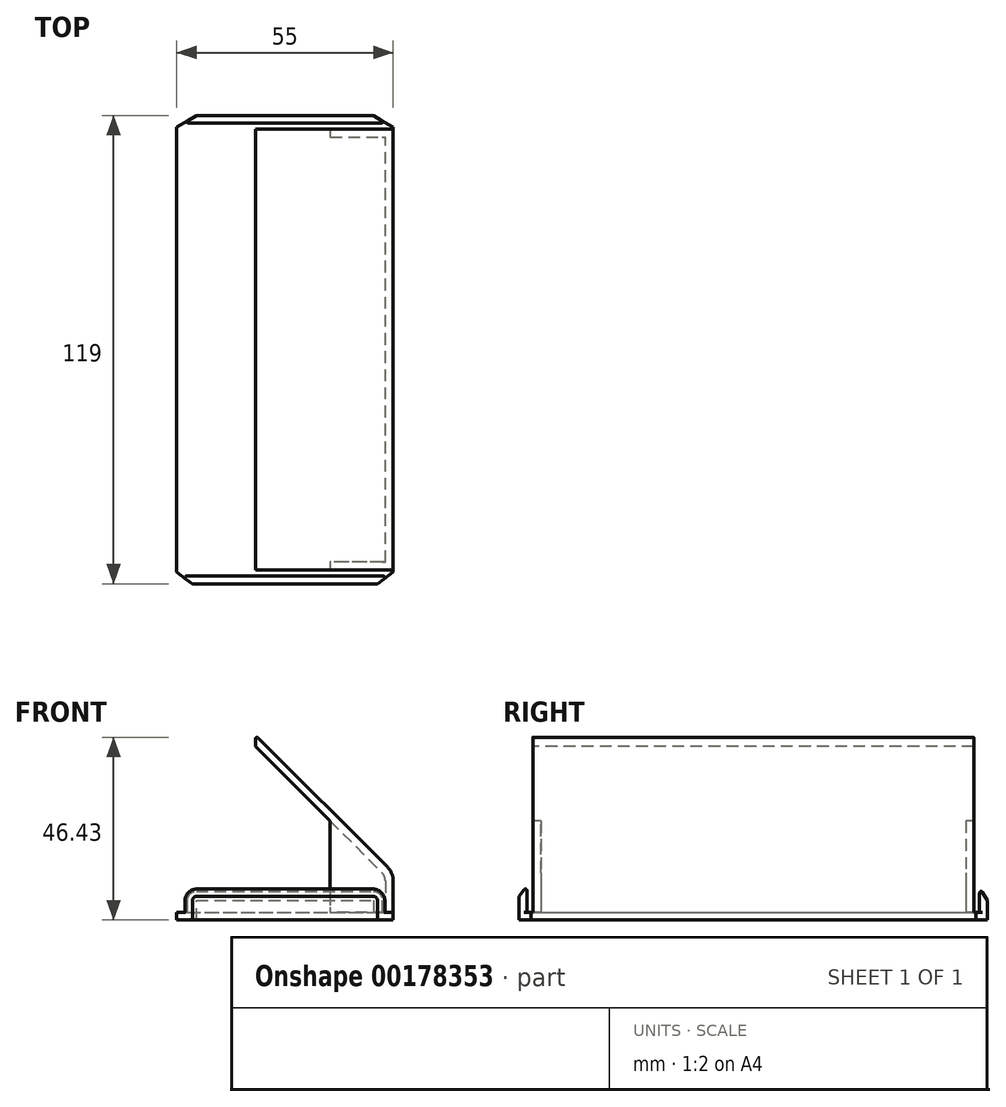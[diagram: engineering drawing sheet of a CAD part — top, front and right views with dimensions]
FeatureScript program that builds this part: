
annotation { "Feature Type Name" : "Feature", "Feature Type Description" : "" }
export const myFeature = defineFeature(function(context is Context, id is Id, definition is map)
    precondition{}
    {
        {
            var Q0;
            Q0=qCreatedBy(makeId("Top.planeOp"),FACE);
            var sketch = newSketch(context, id + "F0", { "sketchPlane" : qUnion([Q0])});
            skLineSegment(sketch, "E0.bottom", {"start": v(27.5, -59.5) * mm, "end": v(-27.5, -59.5) * mm});
            skLineSegment(sketch, "E0.top", {"start": v(27.5, 59.5) * mm, "end": v(-27.5, 59.5) * mm});
            skLineSegment(sketch, "E0.left", {"start": v(27.5, -59.5) * mm, "end": v(27.5, 59.5) * mm});
            skLineSegment(sketch, "E0.right", {"start": v(-27.5, -59.5) * mm, "end": v(-27.5, 59.5) * mm});
            skPoint(sketch, "E0.middle", {"position": v(0, 0) * mm});
            skLineSegment(sketch, "E1", {"start": v(-27.5, 57.5) * mm, "end": v(27.5, 57.5) * mm});
            skLineSegment(sketch, "E2", {"start": v(-27.5, -57.5) * mm, "end": v(27.5, -57.5) * mm});
            skLineSegment(sketch, "E3", {"start": v(-27.5, 56) * mm, "end": v(27.5, 56) * mm});
            skLineSegment(sketch, "E4", {"start": v(-27.5, -56) * mm, "end": v(27.5, -56) * mm});
            skSolve(sketch);
        }
        {
            var Q0;
            {var subQ0=sQuery(id+"F0.wireOp",EDGE,"E3");Q0=makeQuery(id+"F0.imprint","IMPRINT",FACE,{"disambiguationData":[TD([[makeQuery(id+"F0.imprint","IMPRINT",EDGE,{"derivedFrom":subQ0}),-1.0]])]});}
            extrude(context, id + "F1", {"entities" : qUnion([Q0]), "depth" : 47 * mm});
        }
        {
            var Q0;
            {var subQ0=sQuery(id+"F0.wireOp",EDGE,"E1");Q0=makeQuery(id+"F0.imprint","IMPRINT",FACE,{"disambiguationData":[TD([[makeQuery(id+"F0.imprint","IMPRINT",EDGE,{"derivedFrom":subQ0}),-1.0]])]});}
            var Q1;
            {var subQ0=sQuery(id+"F0.wireOp",EDGE,"E2");Q1=makeQuery(id+"F0.imprint","IMPRINT",FACE,{"disambiguationData":[TD([[makeQuery(id+"F0.imprint","IMPRINT",EDGE,{"derivedFrom":subQ0}),1.0]])]});}
            extrude(context, id + "F2", {"entities" : qUnion([Q0, Q1]), "operationType" : NewBodyOperationType.ADD, "depth" : 2 * mm});
        }
        {
            var Q0;
            {var subQ0=sQuery(id+"F0.wireOp",EDGE,"E0.top");Q0=makeQuery(id+"F0.imprint","IMPRINT",FACE,{"disambiguationData":[TD([[makeQuery(id+"F0.imprint","IMPRINT",EDGE,{"derivedFrom":subQ0}),1.0]])]});}
            var Q1;
            {var subQ0=sQuery(id+"F0.wireOp",EDGE,"E0.bottom");Q1=makeQuery(id+"F0.imprint","IMPRINT",FACE,{"disambiguationData":[TD([[makeQuery(id+"F0.imprint","IMPRINT",EDGE,{"derivedFrom":subQ0}),-1.0]])]});}
            extrude(context, id + "F3", {"entities" : qUnion([Q0, Q1]), "operationType" : NewBodyOperationType.ADD, "depth" : 10 * mm});
        }
        {
            var Q0;
            Q0=makeQuery(id+"F1.opExtrude","CAP_EDGE",EDGE,{"disambiguationData":[OSD([sQuery(id+"F0.wireOp",EDGE,"E0.left")])],"isStart":false});
            chamfer(context, id + "F4", {"entities" : qUnion([Q0]), "chamferType" : ChamferType.TWO_OFFSETS, "width1" : 35 * mm, "oppositeDirection" : false, "width2" : 35 * mm, "tangentPropagation" : true});
        }
        {
            var Q0;
            {var subQ0=sQuery(id+"F0.wireOp",EDGE,"E0.right");Q0=makeQuery(id+"F3.opExtrude","CAP_EDGE",EDGE,{"disambiguationData":[OSD([subQ0]),TDD([makeQuery(id+"F0.imprint","IMPRINT",EDGE,{"disambiguationData":[TD([[makeQuery(id+"F0.imprint","INTERSECT",VERTEX,{"derivedFrom":[sQuery(id+"F0.wireOp",EDGE,"E0.bottom"),subQ0]}),-1.0]])],"derivedFrom":subQ0})])],"isStart":false});}
            var Q1;
            {var subQ0=sQuery(id+"F0.wireOp",EDGE,"E0.left");Q1=makeQuery(id+"F3.opExtrude","CAP_EDGE",EDGE,{"disambiguationData":[OSD([subQ0]),TDD([makeQuery(id+"F0.imprint","IMPRINT",EDGE,{"disambiguationData":[TD([[makeQuery(id+"F0.imprint","INTERSECT",VERTEX,{"derivedFrom":[sQuery(id+"F0.wireOp",EDGE,"E0.bottom"),subQ0]}),-1.0]])],"derivedFrom":subQ0})])],"isStart":false});}
            var Q2;
            {var subQ0=sQuery(id+"F0.wireOp",EDGE,"E0.right");Q2=makeQuery(id+"F3.opExtrude","CAP_EDGE",EDGE,{"disambiguationData":[OSD([subQ0]),TDD([makeQuery(id+"F0.imprint","IMPRINT",EDGE,{"disambiguationData":[TD([[makeQuery(id+"F0.imprint","INTERSECT",VERTEX,{"derivedFrom":[sQuery(id+"F0.wireOp",EDGE,"E0.top"),subQ0]}),1.0]])],"derivedFrom":subQ0})])],"isStart":false});}
            var Q3;
            {var subQ0=sQuery(id+"F0.wireOp",EDGE,"E0.left");Q3=makeQuery(id+"F3.opExtrude","CAP_EDGE",EDGE,{"disambiguationData":[OSD([subQ0]),TDD([makeQuery(id+"F0.imprint","IMPRINT",EDGE,{"disambiguationData":[TD([[makeQuery(id+"F0.imprint","INTERSECT",VERTEX,{"derivedFrom":[sQuery(id+"F0.wireOp",EDGE,"E0.top"),subQ0]}),1.0]])],"derivedFrom":subQ0})])],"isStart":false});}
            var Q4;
            {var subQ0=sQuery(id+"F0.wireOp",EDGE,"E0.left");var subQ1=makeQuery(id+"F0.imprint","INTERSECT",VERTEX,{"derivedFrom":[subQ0,sQuery(id+"F0.wireOp",EDGE,"E1")]});var subQ2=makeQuery(id+"F0.imprint","INTERSECT",VERTEX,{"derivedFrom":[subQ0,sQuery(id+"F0.wireOp",EDGE,"E2")]});Q4=makeQuery(id+"F4.opChamfer","BLEND_EDGE",EDGE,{"blendedFrom":[makeQuery(id+"F1.opExtrude","CAP_EDGE",EDGE,{"disambiguationData":[OSD([subQ0])],"isStart":false}),makeQuery(id+"F3.boolean.opBoolean","MERGE",FACE,{"derivedFrom":[makeQuery(id+"F2.boolean.opBoolean","MERGE",FACE,{"derivedFrom":[makeQuery(id+"F1.opExtrude","SWEPT_FACE",FACE,{"disambiguationData":[OSD([subQ0])]}),makeQuery(id+"F2.opExtrude","SWEPT_FACE",FACE,{"disambiguationData":[OSD([subQ0]),TDD([makeQuery(id+"F0.imprint","IMPRINT",EDGE,{"disambiguationData":[TD([[subQ2,-1.0]])],"derivedFrom":subQ0})])]}),makeQuery(id+"F2.opExtrude","SWEPT_FACE",FACE,{"disambiguationData":[OSD([subQ0]),TDD([makeQuery(id+"F0.imprint","IMPRINT",EDGE,{"disambiguationData":[TD([[subQ1,1.0]])],"derivedFrom":subQ0})])]})]}),makeQuery(id+"F3.opExtrude","SWEPT_FACE",FACE,{"disambiguationData":[OSD([subQ0]),TDD([makeQuery(id+"F0.imprint","IMPRINT",EDGE,{"disambiguationData":[TD([[makeQuery(id+"F0.imprint","INTERSECT",VERTEX,{"derivedFrom":[sQuery(id+"F0.wireOp",EDGE,"E0.bottom"),subQ0]}),-1.0]])],"derivedFrom":subQ0})])]}),makeQuery(id+"F3.opExtrude","SWEPT_FACE",FACE,{"disambiguationData":[OSD([subQ0]),TDD([makeQuery(id+"F0.imprint","IMPRINT",EDGE,{"disambiguationData":[TD([[makeQuery(id+"F0.imprint","INTERSECT",VERTEX,{"derivedFrom":[sQuery(id+"F0.wireOp",EDGE,"E0.top"),subQ0]}),1.0]])],"derivedFrom":subQ0})])]})]})],"blendedInto":[makeQuery(id+"F3.boolean.opBoolean","MERGE",FACE,{"derivedFrom":[makeQuery(id+"F2.boolean.opBoolean","MERGE",FACE,{"derivedFrom":[makeQuery(id+"F1.opExtrude","SWEPT_FACE",FACE,{"disambiguationData":[OSD([subQ0])]}),makeQuery(id+"F2.opExtrude","SWEPT_FACE",FACE,{"disambiguationData":[OSD([subQ0]),TDD([makeQuery(id+"F0.imprint","IMPRINT",EDGE,{"disambiguationData":[TD([[subQ2,-1.0]])],"derivedFrom":subQ0})])]}),makeQuery(id+"F2.opExtrude","SWEPT_FACE",FACE,{"disambiguationData":[OSD([subQ0]),TDD([makeQuery(id+"F0.imprint","IMPRINT",EDGE,{"disambiguationData":[TD([[subQ1,1.0]])],"derivedFrom":subQ0})])]})]}),makeQuery(id+"F3.opExtrude","SWEPT_FACE",FACE,{"disambiguationData":[OSD([subQ0]),TDD([makeQuery(id+"F0.imprint","IMPRINT",EDGE,{"disambiguationData":[TD([[makeQuery(id+"F0.imprint","INTERSECT",VERTEX,{"derivedFrom":[sQuery(id+"F0.wireOp",EDGE,"E0.bottom"),subQ0]}),-1.0]])],"derivedFrom":subQ0})])]}),makeQuery(id+"F3.opExtrude","SWEPT_FACE",FACE,{"disambiguationData":[OSD([subQ0]),TDD([makeQuery(id+"F0.imprint","IMPRINT",EDGE,{"disambiguationData":[TD([[makeQuery(id+"F0.imprint","INTERSECT",VERTEX,{"derivedFrom":[sQuery(id+"F0.wireOp",EDGE,"E0.top"),subQ0]}),1.0]])],"derivedFrom":subQ0})])]})]})]});}
            var Q5;
            {var subQ0=sQuery(id+"F0.wireOp",EDGE,"E0.top");Q5=makeQuery(id+"F10.opChamfer","BLEND_EDGE",EDGE,{"blendedFrom":[makeQuery(id+"F3.opExtrude","CAP_EDGE",EDGE,{"disambiguationData":[OSD([subQ0])],"isStart":false}),makeQuery(id+"F3.opExtrude","SWEPT_FACE",FACE,{"disambiguationData":[OSD([subQ0])]})],"blendedInto":[makeQuery(id+"F3.opExtrude","SWEPT_FACE",FACE,{"disambiguationData":[OSD([subQ0])]})]});}
            var Q6;
            {var subQ0=sQuery(id+"F0.wireOp",EDGE,"E0.bottom");Q6=makeQuery(id+"F11.opChamfer","BLEND_EDGE",EDGE,{"blendedFrom":[makeQuery(id+"F3.opExtrude","CAP_EDGE",EDGE,{"disambiguationData":[OSD([subQ0])],"isStart":false}),makeQuery(id+"F3.opExtrude","SWEPT_FACE",FACE,{"disambiguationData":[OSD([subQ0])]})],"blendedInto":[makeQuery(id+"F3.opExtrude","SWEPT_FACE",FACE,{"disambiguationData":[OSD([subQ0])]})]});}
            fillet(context, id + "F5", {"entities" : qUnion([Q0, Q1, Q2, Q3, Q4, Q5, Q6]), "radius" : 5 * mm, "tangentPropagation" : true, "allowEdgeOverflow" : false});
        }
        {
            var Q0;
            Q0=makeQuery(id+"F1.opExtrude","CAP_FACE",FACE,{"disambiguationData":[OSD([sQuery(id+"F0.wireOp",EDGE,"E0.left"),sQuery(id+"F0.wireOp",EDGE,"E0.right"),sQuery(id+"F0.wireOp",EDGE,"E3"),sQuery(id+"F0.wireOp",EDGE,"E4")])],"isStart":false});
            extrude(context, id + "F6", {"entities" : qUnion([Q0]), "operationType" : NewBodyOperationType.REMOVE, "oppositeDirection" : true, "depth" : 43 * mm});
        }
        {
            var Q0;
            Q0=makeQuery(id+"F1.opExtrude","SWEPT_FACE",FACE,{"disambiguationData":[OSD([sQuery(id+"F0.wireOp",EDGE,"E4")])]});
            var sketch = newSketch(context, id + "F7", { "sketchPlane" : qUnion([Q0])});
            skLineSegment(sketch, "E5", {"start": v(-7.5, 44.17) * mm, "end": v(11.5, 25.17) * mm});
            skLineSegment(sketch, "E6", {"start": v(11.5, 25.17) * mm, "end": v(11.5, 0) * mm});
            skSolve(sketch);
        }
        {
            var Q0;
            {var subQ0=sQuery(id+"F7.wireOp",EDGE,"E5");Q0=makeQuery(id+"F7.imprint","IMPRINT",FACE,{"disambiguationData":[TD([[makeQuery(id+"F7.imprint","IMPRINT",EDGE,{"derivedFrom":subQ0}),-1.0]])]});}
            extrude(context, id + "F8", {"entities" : qUnion([Q0]), "operationType" : NewBodyOperationType.REMOVE, "endBound" : BoundingType.UP_TO_NEXT, "oppositeDirection" : true, "depth" : 25 * mm});
        }
        {
            var Q0;
            Q0=makeQuery(id+"F8.boolean.opBoolean","COPY",FACE,{"derivedFrom":makeQuery(id+"F8.opExtrude","SWEPT_FACE",FACE,{"disambiguationData":[OSD([sQuery(id+"F7.wireOp",EDGE,"E6")])]})});
            shell(context, id + "F9", {"entities" : qUnion([Q0]), "thickness" : 2 * mm});
        }
        {
            var Q0;
            Q0=makeQuery(id+"F3.opExtrude","CAP_EDGE",EDGE,{"disambiguationData":[OSD([sQuery(id+"F0.wireOp",EDGE,"E0.top")])],"isStart":false});
            chamfer(context, id + "F10", {"entities" : qUnion([Q0]), "chamferType" : ChamferType.TWO_OFFSETS, "width1" : 3 * mm, "oppositeDirection" : false, "width2" : 5 * mm, "tangentPropagation" : true});
        }
        {
            var Q0;
            Q0=makeQuery(id+"F3.opExtrude","CAP_EDGE",EDGE,{"disambiguationData":[OSD([sQuery(id+"F0.wireOp",EDGE,"E0.bottom")])],"isStart":false});
            chamfer(context, id + "F11", {"entities" : qUnion([Q0]), "chamferType" : ChamferType.TWO_OFFSETS, "width1" : 4 * mm, "oppositeDirection" : false, "width2" : 3 * mm, "tangentPropagation" : true});
        }
        {
            var Q0;
            {var subQ0=sQuery(id+"F0.wireOp",EDGE,"E4");var subQ1=sQuery(id+"F0.wireOp",EDGE,"E3");var subQ2=sQuery(id+"F0.wireOp",EDGE,"E0.right");var subQ3=sQuery(id+"F0.wireOp",EDGE,"E0.left");Q0=makeQuery(id+"F6.boolean.opBoolean","MERGE",EDGE,{"derivedFrom":[makeQuery(id+"F4.opChamfer","BLEND_EDGE",EDGE,{"blendedFrom":[makeQuery(id+"F1.opExtrude","CAP_EDGE",EDGE,{"disambiguationData":[OSD([subQ3])],"isStart":false}),makeQuery(id+"F1.opExtrude","CAP_FACE",FACE,{"disambiguationData":[OSD([subQ3,subQ2,subQ1,subQ0])],"isStart":false})],"blendedInto":[makeQuery(id+"F1.opExtrude","CAP_FACE",FACE,{"disambiguationData":[OSD([subQ3,subQ2,subQ1,subQ0])],"isStart":false})]}),makeQuery(id+"F6.opExtrude","CAP_EDGE",EDGE,{"disambiguationData":[OSD([subQ3,subQ2,subQ1,subQ0])],"isStart":true})]});}
            var Q1;
            Q1=makeQuery(id+"F10.opChamfer","BLEND_EDGE",EDGE,{"blendedFrom":[makeQuery(id+"F3.opExtrude","CAP_EDGE",EDGE,{"disambiguationData":[OSD([sQuery(id+"F0.wireOp",EDGE,"E0.top")])],"isStart":false}),makeQuery(id+"F3.opExtrude","SWEPT_FACE",FACE,{"disambiguationData":[OSD([sQuery(id+"F0.wireOp",EDGE,"E1")])]})],"blendedInto":[makeQuery(id+"F3.opExtrude","SWEPT_FACE",FACE,{"disambiguationData":[OSD([sQuery(id+"F0.wireOp",EDGE,"E1")])]})]});
            var Q2;
            Q2=makeQuery(id+"F11.opChamfer","BLEND_EDGE",EDGE,{"blendedFrom":[makeQuery(id+"F3.opExtrude","CAP_EDGE",EDGE,{"disambiguationData":[OSD([sQuery(id+"F0.wireOp",EDGE,"E0.bottom")])],"isStart":false}),makeQuery(id+"F3.opExtrude","SWEPT_FACE",FACE,{"disambiguationData":[OSD([sQuery(id+"F0.wireOp",EDGE,"E2")])]})],"blendedInto":[makeQuery(id+"F3.opExtrude","SWEPT_FACE",FACE,{"disambiguationData":[OSD([sQuery(id+"F0.wireOp",EDGE,"E2")])]})]});
            fillet(context, id + "F12", {"entities" : qUnion([Q0, Q1, Q2]), "radius" : 0.4 * mm, "tangentPropagation" : true, "allowEdgeOverflow" : false});
        }
    });
